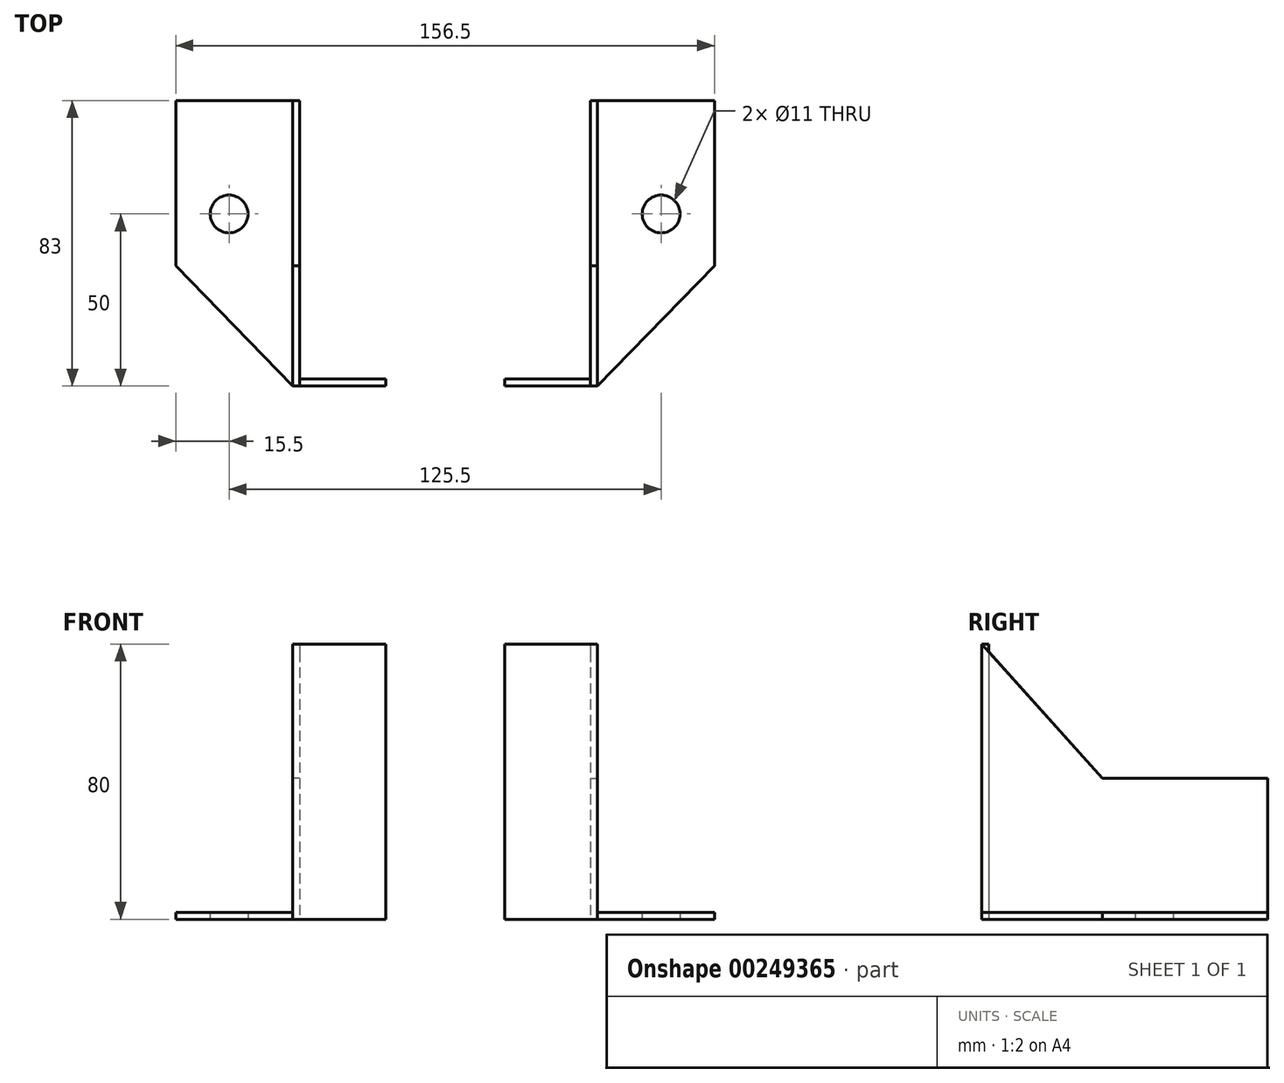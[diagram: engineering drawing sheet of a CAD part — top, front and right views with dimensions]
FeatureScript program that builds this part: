
annotation { "Feature Type Name" : "Feature", "Feature Type Description" : "" }
export const myFeature = defineFeature(function(context is Context, id is Id, definition is map)
    precondition{}
    {
        {
            assignVariable(context, id + "F0", {"name" : "metal_thickness", "anyValue" : 2});
        }
        {
            assignVariable(context, id + "F1", {"name" : "gap", "anyValue" : 0.5});
        }
        {
            var Q0;
            Q0=qCreatedBy(makeId("Top.planeOp"),FACE);
            var sketch = newSketch(context, id + "F2", { "sketchPlane" : qUnion([Q0])});
            skLineSegment(sketch, "E0", {"start": v(0, 48) * mm, "end": v(-34, 48) * mm});
            skLineSegment(sketch, "E1", {"start": v(-34, 48) * mm, "end": v(-34, 0) * mm});
            skLineSegment(sketch, "E2", {"start": v(-34, 0) * mm, "end": v(0, -35) * mm});
            skLineSegment(sketch, "E3", {"start": v(0, -35) * mm, "end": v(0, 48) * mm});
            skLineSegment(sketch, "E4", {"start": v(2, 48) * mm, "end": v(0, 48) * mm});
            skLineSegment(sketch, "E5", {"start": v(2, -35) * mm, "end": v(2, 48) * mm});
            skLineSegment(sketch, "E6", {"start": v(0, -35) * mm, "end": v(2, -35) * mm});
            skLineSegment(sketch, "E7", {"start": v(2, -33) * mm, "end": v(27, -33) * mm});
            skLineSegment(sketch, "E8", {"start": v(2, -35) * mm, "end": v(27, -35) * mm});
            skLineSegment(sketch, "E9", {"start": v(27, -35) * mm, "end": v(27, -33) * mm});
            skCircle(sketch, "E10", {"center": v(-18.5, 15) * mm, "radius": 5.5 * mm});
            skSolve(sketch);
        }
        {
            var Q0;
            Q0=makeQuery(id+"F2.imprint","IMPRINT",FACE,{"disambiguationData":[TD([[makeQuery(id+"F2.imprint","IMPRINT",EDGE,{"derivedFrom":sQuery(id+"F2.wireOp",EDGE,"E3")}),-1.0]])]});
            extrude(context, id + "F3", {"entities" : qUnion([Q0]), "depth" : 80 * mm});
        }
        {
            var Q0;
            Q0=makeQuery(id+"F2.imprint","IMPRINT",FACE,{"disambiguationData":[TD([[makeQuery(id+"F2.imprint","IMPRINT",EDGE,{"derivedFrom":sQuery(id+"F2.wireOp",EDGE,"E0")}),1.0]])]});
            extrude(context, id + "F4", {"entities" : qUnion([Q0]), "operationType" : NewBodyOperationType.ADD, "depth" : (getVariable(context, 'metal_thickness')) * mm});
        }
        {
            var Q0;
            Q0=makeQuery(id+"F3.opExtrude","SWEPT_FACE",FACE,{"disambiguationData":[OSD([sQuery(id+"F2.wireOp",EDGE,"E3")])]});
            var sketch = newSketch(context, id + "F5", { "sketchPlane" : qUnion([Q0])});
            skLineSegment(sketch, "E11", {"start": v(-48, 2) * mm, "end": v(-48, 41) * mm});
            skLineSegment(sketch, "E12", {"start": v(-48, 41) * mm, "end": v(0, 41) * mm});
            skLineSegment(sketch, "E13", {"start": v(0, 41) * mm, "end": v(35, 80) * mm});
            skSolve(sketch);
        }
        {
            var Q0;
            {var subQ0=sQuery(id+"F5.wireOp",EDGE,"E12");Q0=makeQuery(id+"F5.imprint","IMPRINT",FACE,{"disambiguationData":[TD([[makeQuery(id+"F5.imprint","IMPRINT",EDGE,{"derivedFrom":subQ0}),1.0]])]});}
            extrude(context, id + "F6", {"entities" : qUnion([Q0]), "operationType" : NewBodyOperationType.REMOVE, "endBound" : BoundingType.UP_TO_NEXT, "oppositeDirection" : true, "depth" : 25 * mm});
        }
        {
            var Q0;
            {var subQ2=sQuery(id+"F2.wireOp",EDGE,"E7");Q0=makeQuery(id+"F2.imprint","IMPRINT",FACE,{"disambiguationData":[TD([[makeQuery(id+"F2.imprint","IMPRINT",EDGE,{"derivedFrom":subQ2}),-1.0]])]});}
            extrude(context, id + "F7", {"entities" : qUnion([Q0]), "operationType" : NewBodyOperationType.ADD, "depth" : 80 * mm});
        }
        {
            var Q0;
            Q0=makeQuery(id+"F2.imprint","IMPRINT",FACE,{"disambiguationData":[TD([[makeQuery(id+"F2.imprint","IMPRINT",EDGE,{"derivedFrom":sQuery(id+"F2.wireOp",EDGE,"E10")}),1.0]])]});
            extrude(context, id + "F8", {"entities" : qUnion([Q0]), "operationType" : NewBodyOperationType.REMOVE, "endBound" : BoundingType.THROUGH_ALL, "depth" : 25 * mm});
        }
        {
            var Q0;
            Q0=makeQuery(id+"F3.opExtrude","SWEPT_BODY",BODY,{"disambiguationData":[OSD([sQuery(id+"F2.wireOp",EDGE,"E3"),sQuery(id+"F2.wireOp",EDGE,"E4"),sQuery(id+"F2.wireOp",EDGE,"E5"),sQuery(id+"F2.wireOp",EDGE,"E6")])]});
            var Q1;
            Q1=qCreatedBy(makeId("Right.planeOp"),FACE);
            mirror(context, id + "F9", {"entities" : qUnion([Q0]), "mirrorPlane" : qUnion([Q1])});
        }
        {
            var Q0;
            Q0=makeQuery(id+"F9.opPattern","COPY",BODY,{"derivedFrom":makeQuery(id+"F3.opExtrude","SWEPT_BODY",BODY,{"disambiguationData":[OSD([sQuery(id+"F2.wireOp",EDGE,"E3"),sQuery(id+"F2.wireOp",EDGE,"E4"),sQuery(id+"F2.wireOp",EDGE,"E5"),sQuery(id+"F2.wireOp",EDGE,"E6")])]}),"instanceName":"1"});
            transform(context, id + "F10", {"entities" : qUnion([Q0]), "transformType" : TransformType.TRANSLATION_3D, "dx" : (84 + getVariable(context, 'metal_thickness') * 2 + getVariable(context, 'gap')) * mm, "dy" : 0 * mm, "dz" : 0 * mm, "makeCopy" : false});
        }
    });
